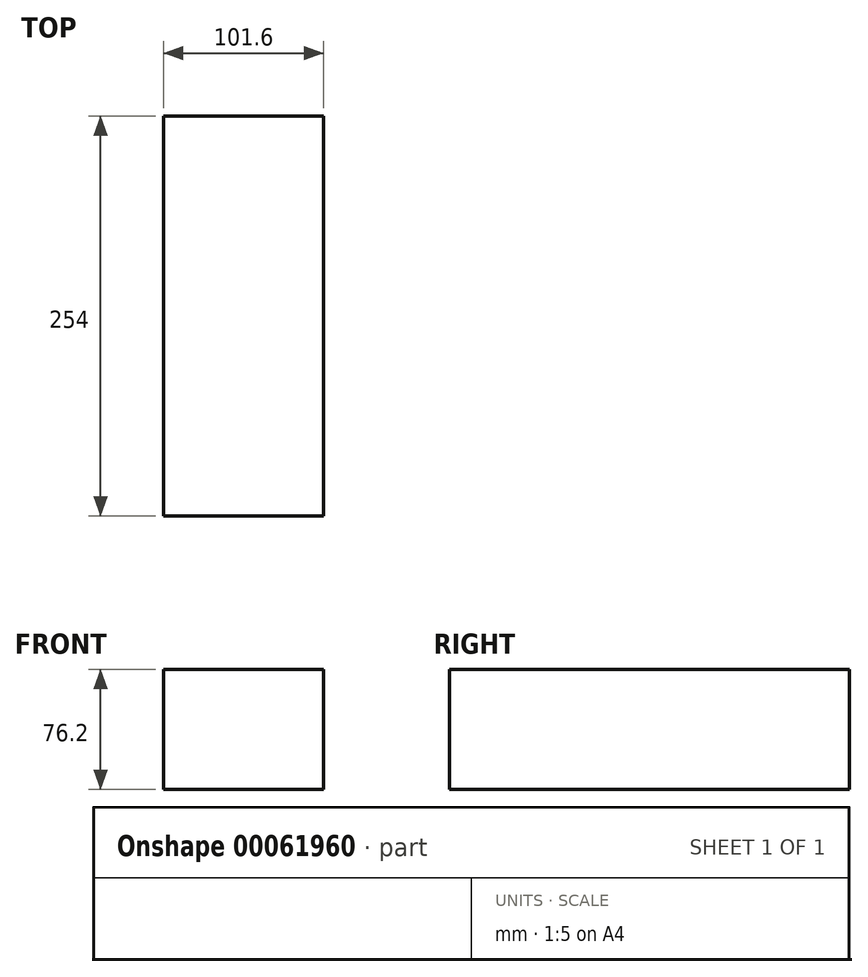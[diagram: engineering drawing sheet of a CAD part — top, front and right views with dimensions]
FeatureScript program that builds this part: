
annotation { "Feature Type Name" : "Feature", "Feature Type Description" : "" }
export const myFeature = defineFeature(function(context is Context, id is Id, definition is map)
    precondition{}
    {
        {
            var Q0;
            Q0=qCreatedBy(makeId("Front.planeOp"),FACE);
            var sketch = newSketch(context, id + "F2", { "sketchPlane" : qUnion([Q0])});
            skLineSegment(sketch, "E0.rect.bottom", {"start": v(50.8, 38.1) * mm, "end": v(-50.8, 38.1) * mm});
            skLineSegment(sketch, "E0.rect.top", {"start": v(50.8, -38.1) * mm, "end": v(-50.8, -38.1) * mm});
            skLineSegment(sketch, "E0.rect.left", {"start": v(50.8, 38.1) * mm, "end": v(50.8, -38.1) * mm});
            skLineSegment(sketch, "E0.rect.right", {"start": v(-50.8, 38.1) * mm, "end": v(-50.8, -38.1) * mm});
            skPoint(sketch, "E0.rect.middle", {"position": v(0, 0) * mm});
            skSolve(sketch);
        }
        {
            var Q0;
            Q0 = qSketchRegion(id + "F2", true);
            extrude(context, id + "F0", {"entities" : qUnion([Q0]), "endBound" : BoundingType.SYMMETRIC, "depth" : 254 * mm});
        }
    });
